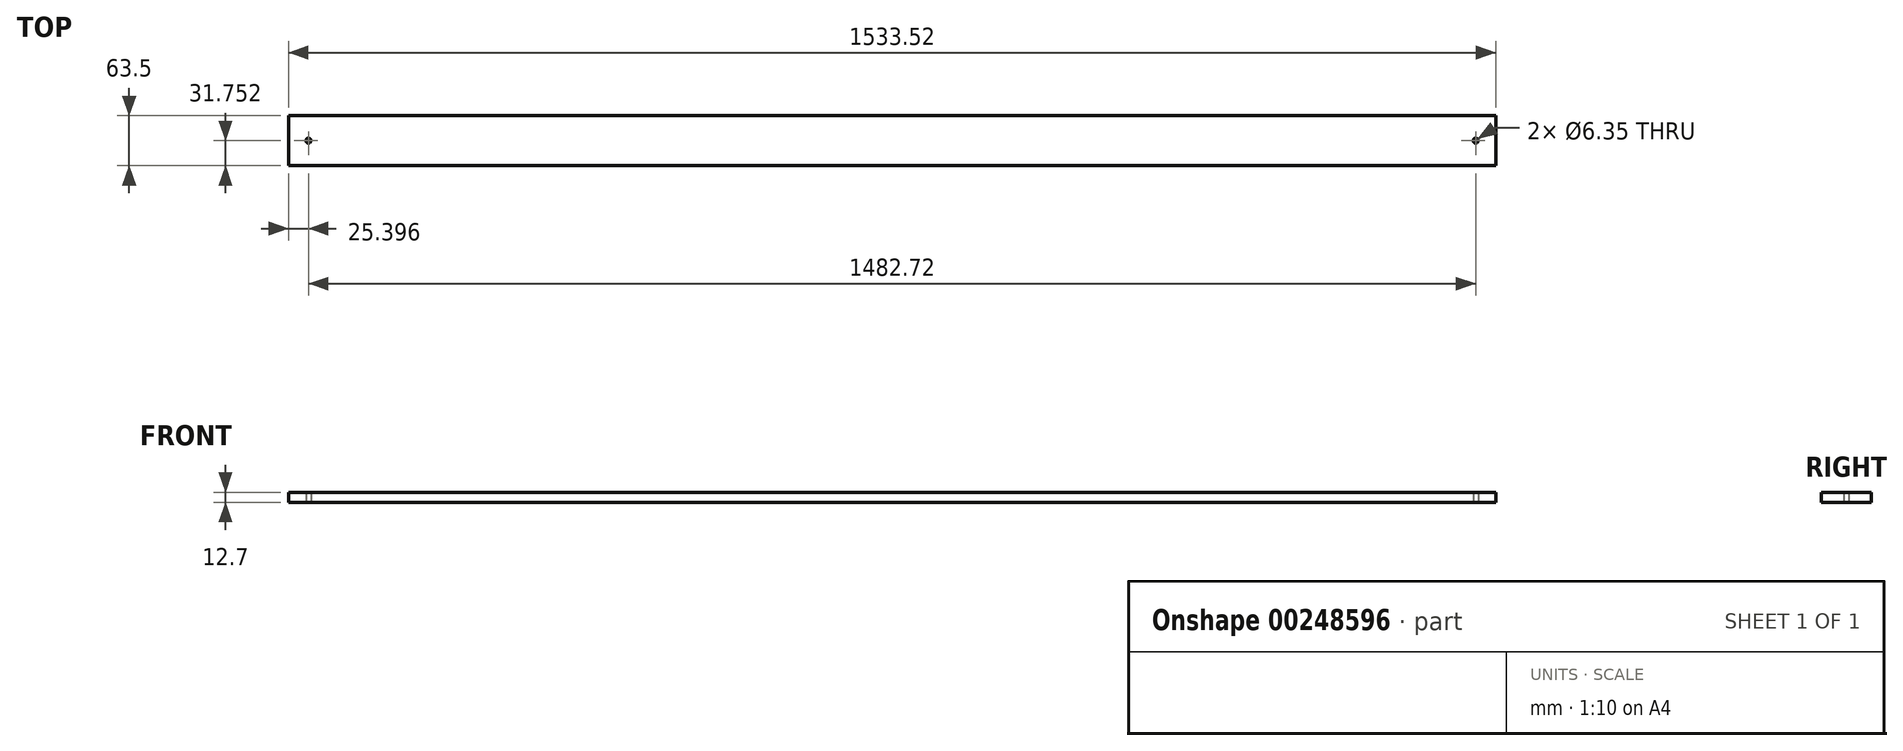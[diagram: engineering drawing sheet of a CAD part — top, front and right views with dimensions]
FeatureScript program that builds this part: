
annotation { "Feature Type Name" : "Feature", "Feature Type Description" : "" }
export const myFeature = defineFeature(function(context is Context, id is Id, definition is map)
    precondition{}
    {
        {
            var Q0;
            Q0=qCreatedBy(makeId("Top.planeOp"),FACE);
            var sketch = newSketch(context, id + "F0", { "sketchPlane" : qUnion([Q0])});
            skLineSegment(sketch, "E0.bottom", {"start": v(-932.78, 44.83) * mm, "end": v(600.74, 44.83) * mm});
            skLineSegment(sketch, "E0.top", {"start": v(-932.78, -18.67) * mm, "end": v(600.74, -18.67) * mm});
            skLineSegment(sketch, "E0.left", {"start": v(-932.78, 44.83) * mm, "end": v(-932.78, -18.67) * mm});
            skLineSegment(sketch, "E0.right", {"start": v(600.74, 44.83) * mm, "end": v(600.74, -18.67) * mm});
            skCircle(sketch, "E1", {"center": v(-907.38, 13.08) * mm, "radius": 3.18 * mm});
            skLineSegment(sketch, "E2", {"start": v(-932.78, 13.08) * mm, "end": v(-859.79, 13.08) * mm, "construction": true});
            skLineSegment(sketch, "E3", {"start": v(600.74, 13.08) * mm, "end": v(481.3, 13.08) * mm, "construction": true});
            skCircle(sketch, "E4", {"center": v(575.34, 13.08) * mm, "radius": 3.18 * mm});
            skSolve(sketch);
        }
        {
            var Q0;
            Q0=makeQuery(id+"F0.imprint","IMPRINT",FACE,{"disambiguationData":[TD([[makeQuery(id+"F0.imprint","IMPRINT",EDGE,{"derivedFrom":sQuery(id+"F0.wireOp",EDGE,"E0.bottom")}),-1.0]])]});
            extrude(context, id + "F1", {"entities" : qUnion([Q0]), "depth" : 12.7 * mm});
        }
    });
